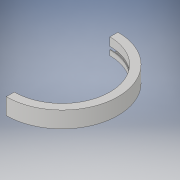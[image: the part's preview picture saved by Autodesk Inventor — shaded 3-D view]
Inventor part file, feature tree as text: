
AUTODESK INVENTOR PART (.ipt)
format: ipt  version: 2017 (Build 210142000, 142)  size: 139,776 bytes
history: native  units: in
note: dims shown in document units (in); Inventor stores cm internally (conversion verified against a paired STEP export)
features: revolve x1, sketch x1
ambient origin geometry x8: Origin, YZ Plane, XZ Plane, XY Plane, X Axis, Y Axis, Z Axis, Center Point
bodies: Solid1 (feature_tree)
feature tree (2):
  revolve  "Revolution1"  [1 undecoded]
  sketch  "Sketch1"  dims[d1=0.8661in d2=5.1195in d3=1.7489in d4=0.0in d5=0.0625in d6=0.0625in d7=0.0625in d8=0.0625in d9=0.7182in d10=0.3125in d11=0.1562in d12=180.0deg]
note: 1 required parameter value undecoded (feature->parameter linkage not recoverable at this tier; creation-order binding heuristic only, values carry confidence <= 0.55)
